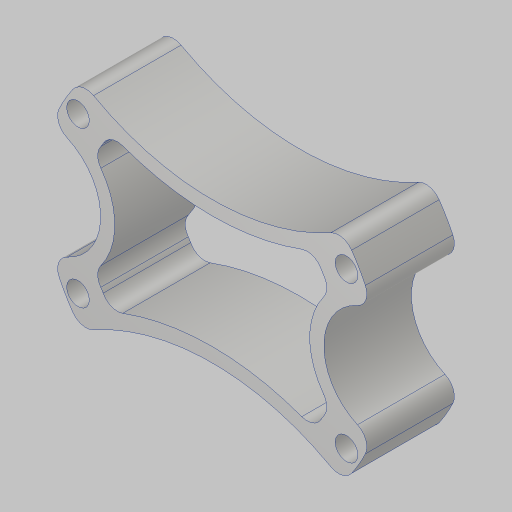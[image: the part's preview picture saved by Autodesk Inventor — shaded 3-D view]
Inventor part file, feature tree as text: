
AUTODESK INVENTOR PART (.ipt)
format: ipt  version: 2023.5 (Build 275446000, 446)  size: 254,976 bytes
history: native  units: in
note: dims shown in document units (in); Inventor stores cm internally (conversion verified against a paired STEP export)
features: sketch x3, extrude x3, fillet x1, hole x1
ambient origin geometry x8: Origin, YZ Plane, XZ Plane, XY Plane, X Axis, Y Axis, Z Axis, Center Point
bodies: Solid1 (feature_tree)
feature tree (8):
  sketch  "Sketch1"  dims[d0=2.375in d1=1.375in d2=0.5in]
  extrude  "Extrusion1"  Depth=0.5in
  fillet  "Fillet1"  Radius=0.5in
  hole  "Hole1"  [1 undecoded]
  extrude  "Extrusion2"  Depth=0.25in
  extrude  "Extrusion3"  Depth=0.5in
  sketch  "Sketch3"  dims[d3=0.5in d4=0.5in]
  sketch  "Sketch4"  dims[d5=0.5in d6=1.25in d7=0.5in d8=0.5in d9=0.125in d10=0.125in d11=1.625in d12=0.0in d13=0.14in d14=0.201in d15=0.75in d16=0.385in d17=0.25in d18=0.5635in d19=1.0in d20=0.8108in d21=1.885in d22=0.125in d23=0.0in d24=0.125in d25=0.125in d26=0.125in d27=3.0in d28=1.0in d29=0.851in d30=0.0in]
note: 1 required parameter value undecoded (feature->parameter linkage not recoverable at this tier; creation-order binding heuristic only, values carry confidence <= 0.55)
